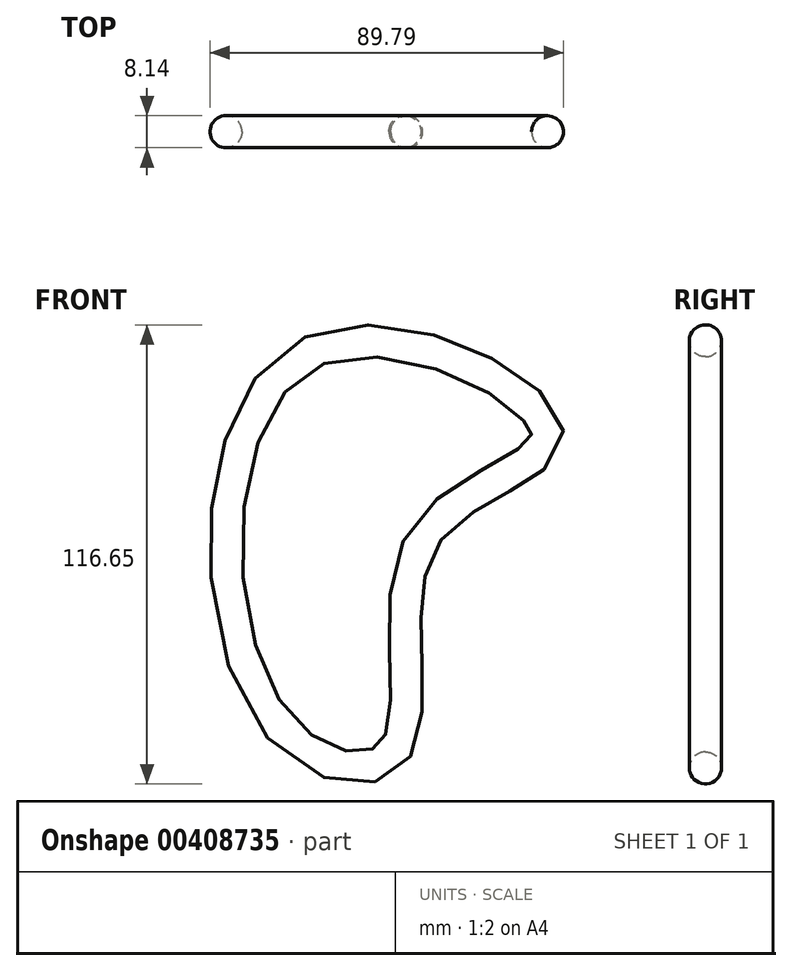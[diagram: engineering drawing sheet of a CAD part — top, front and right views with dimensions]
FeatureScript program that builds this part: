
annotation { "Feature Type Name" : "Feature", "Feature Type Description" : "" }
export const myFeature = defineFeature(function(context is Context, id is Id, definition is map)
    precondition{}
    {
        {
            var Q0;
            Q0=qCreatedBy(makeId("Front.planeOp"),FACE);
            var sketch = newSketch(context, id + "F0", { "sketchPlane" : qUnion([Q0])});
            skFitSpline(sketch, "E0", {"points": [v(-24.34, -34.54) * mm, v(-14.1, 57.13) * mm, v(46.07, 36.7) * mm, v(14.58, 10.32) * mm, v(7.4, -43.88) * mm, v(-24.34, -34.54) * mm]});
            skSolve(sketch);
        }
        {
            var Q0;
            Q0=qCreatedBy(makeId("Top.planeOp"),FACE);
            var sketch = newSketch(context, id + "F1", { "sketchPlane" : qUnion([Q0])});
            skCircle(sketch, "E1", {"center": v(-35.12, 0) * mm, "radius": 4.07 * mm});
            skSolve(sketch);
        }
        {
            var Q0;
            Q0=makeQuery(id+"F1.imprint","IMPRINT",FACE,{"disambiguationData":[TD([[makeQuery(id+"F1.imprint","IMPRINT",EDGE,{"derivedFrom":sQuery(id+"F1.wireOp",EDGE,"E1")}),1.0]])]});
            var Q1;
            Q1=sQuery(id+"F0.wireOp",EDGE,"E0");
            sweep(context, id + "F2", {"profiles" : qUnion([Q0]), "path" : qUnion([Q1])});
        }
    });
